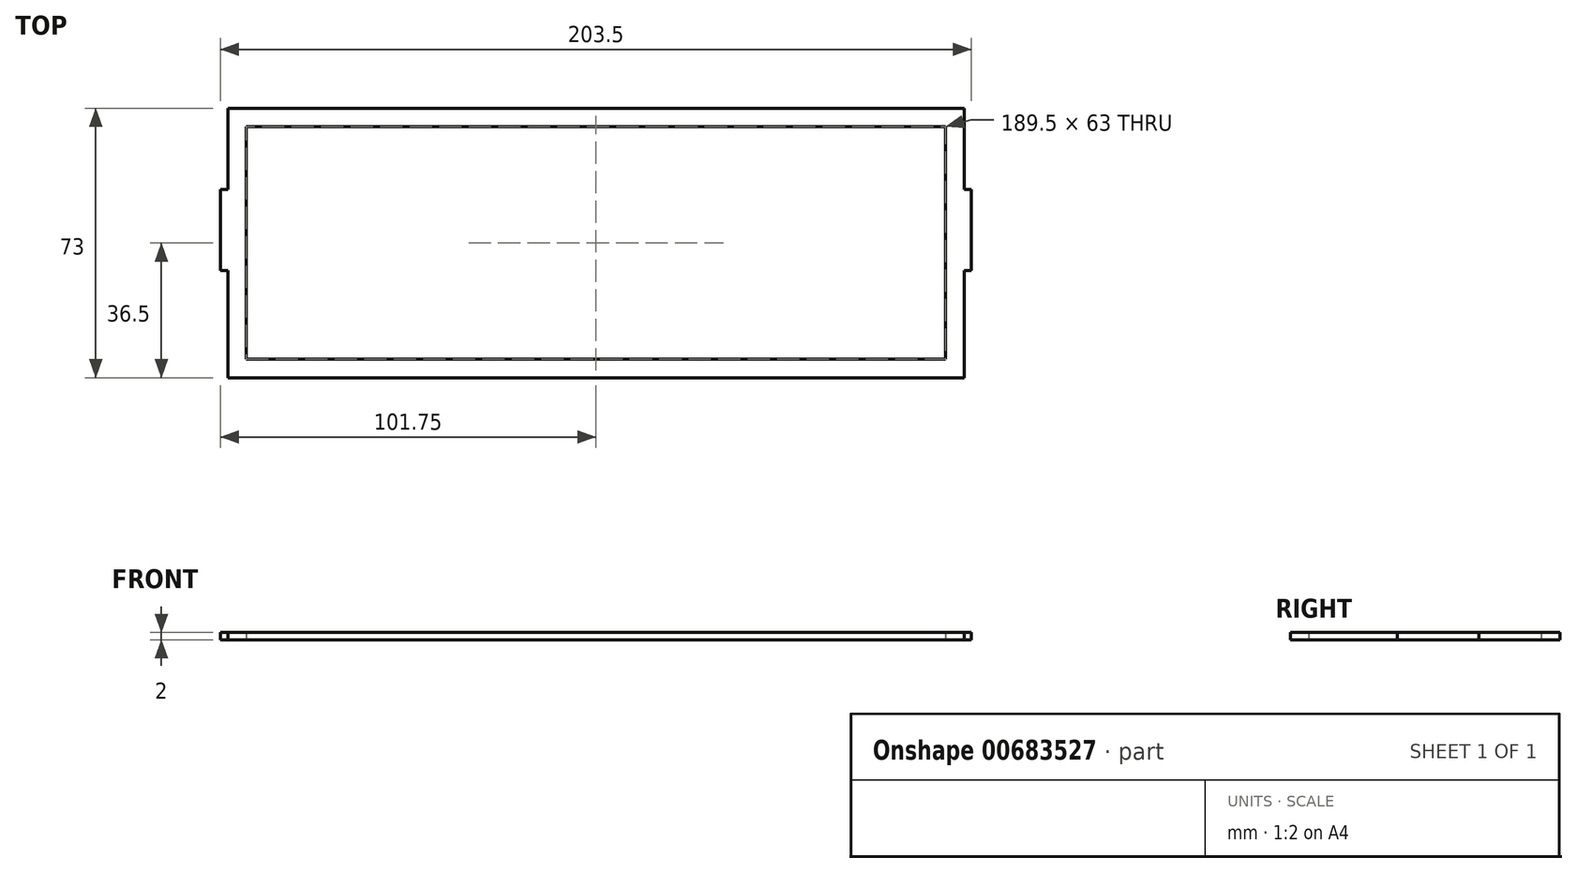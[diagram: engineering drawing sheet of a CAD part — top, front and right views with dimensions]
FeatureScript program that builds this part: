
annotation { "Feature Type Name" : "Feature", "Feature Type Description" : "" }
export const myFeature = defineFeature(function(context is Context, id is Id, definition is map)
    precondition{}
    {
        {
            var Q0;
            Q0=qCreatedBy(makeId("Top.planeOp"),FACE);
            var sketch = newSketch(context, id + "F0", { "sketchPlane" : qUnion([Q0])});
            skLineSegment(sketch, "E0", {"start": v(-103, 73) * mm, "end": v(-103, 51) * mm});
            skLineSegment(sketch, "E1", {"start": v(-103, 51) * mm, "end": v(-105, 51) * mm});
            skLineSegment(sketch, "E2", {"start": v(-103, 29) * mm, "end": v(-105, 29) * mm});
            skLineSegment(sketch, "E3", {"start": v(-105, 51) * mm, "end": v(-105, 29) * mm});
            skLineSegment(sketch, "E4", {"start": v(-103, 29) * mm, "end": v(-103, 0) * mm});
            skLineSegment(sketch, "E5", {"start": v(96.5, 73) * mm, "end": v(96.5, 51) * mm});
            skLineSegment(sketch, "E6", {"start": v(96.5, 51) * mm, "end": v(98.5, 51) * mm});
            skLineSegment(sketch, "E7", {"start": v(96.5, 29) * mm, "end": v(98.5, 29) * mm});
            skLineSegment(sketch, "E8", {"start": v(98.5, 51) * mm, "end": v(98.5, 29) * mm});
            skLineSegment(sketch, "E9", {"start": v(96.5, 29) * mm, "end": v(96.5, 0) * mm});
            skLineSegment(sketch, "E10", {"start": v(-103, 73) * mm, "end": v(96.5, 73) * mm});
            skLineSegment(sketch, "E11", {"start": v(96.5, 0) * mm, "end": v(-103, 0) * mm});
            skLineSegment(sketch, "E12", {"start": v(-98, 68) * mm, "end": v(91.5, 68) * mm});
            skLineSegment(sketch, "E13", {"start": v(91.5, 68) * mm, "end": v(91.5, 5) * mm});
            skLineSegment(sketch, "E14", {"start": v(91.5, 5) * mm, "end": v(-98, 5) * mm});
            skLineSegment(sketch, "E15", {"start": v(-98, 5) * mm, "end": v(-98, 68) * mm});
            skSolve(sketch);
        }
        {
            var Q0;
            Q0 = qSketchRegion(id + "F0", true);
            extrude(context, id + "F1", {"entities" : qUnion([Q0]), "depth" : 2 * mm, "offsetDistance" : 25 * mm});
        }
    });
